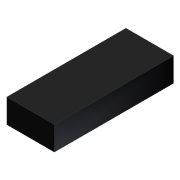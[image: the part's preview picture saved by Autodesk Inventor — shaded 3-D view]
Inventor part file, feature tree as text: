
AUTODESK INVENTOR PART (.ipt)
format: ipt  version: unknown  size: 164,864 bytes
history: native  units: mm
features: extrude x1, sketch x1
ambient origin geometry x8: Origin, YZ Plane, XZ Plane, XY Plane, X Axis, Y Axis, Z Axis, Center Point
feature tree (2):
  extrude  "Выдавливание2"  Depth=3.0mm
  sketch  "Эскиз2"
